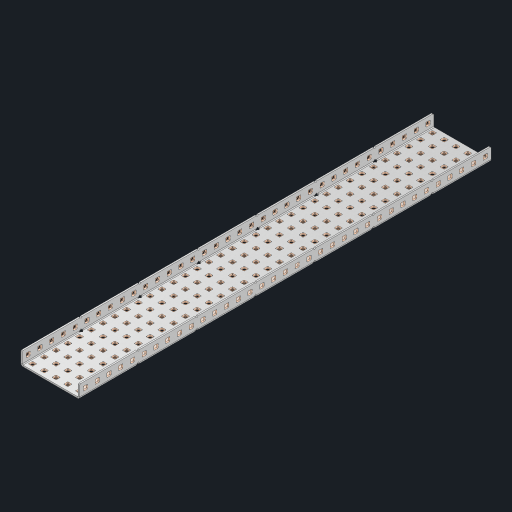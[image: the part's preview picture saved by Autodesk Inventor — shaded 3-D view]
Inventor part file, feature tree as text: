
AUTODESK INVENTOR PART (.ipt)
format: ipt  version: 2023 (Build 270158000, 158)  size: 2,543,616 bytes
history: native  units: in
note: dims shown in document units (in); Inventor stores cm internally (conversion verified against a paired STEP export)
features: other x250, extrude x244, sheet_metal_op x10, sketch x8, mirror x1, pattern_linear x1, chamfer x1
ambient origin geometry x8: Origin, YZ Plane, XZ Plane, XY Plane, X Axis, Y Axis, Z Axis, Center Point
bodies: Solid1 (feature_tree), Body (feature_tree)
feature tree (515):
  other  "Flange Pattern Plane"
  sheet_metal_op  "Flange Pattern"
  sheet_metal_op  "Body Pattern"
  other  "Arc Length"
  mirror  "Notch Mirror"
  pattern_linear  "Notch Pattern"  Spacing1=0.25in  [1 undecoded]
  chamfer  "End Chamfer"
  extrude  "Half Cut"  Depth=0.0625in
  sketch  "Sketch1"  dims[d0=2.5in]
  other  "Plate1"
  sketch  "Sketch2"  dims[d1=17.5in]
  other  "Plate2"
  sheet_metal_op  "Bend1"
  sheet_metal_op  "Corner1"
  sketch  "Sketch3"  dims[d2=0.0625in]
  other  "Flange Pattern Sketch"
  sketch  "Sketch7"  dims[d3=0.0625in]
  other  "Srf1"
  other  "Srf2"
  sketch  "Sketch8"  dims[d4=0.0312in]
  sketch  "Sketch9"  dims[d5=0.125in]
  other  "Srf91"
  sheet_metal_op  "Body Pattern Sketch"
  other  "Srf92"
  sketch  "Sketch13"  dims[d6=0.0625in]
  sketch  "Sketch14"  dims[d7=0.5in d8=90.0deg d9=0.0312in d10=0.25in d11=0.0625in d12=0.0625in d16=0.182in d17=0.02in d18=0.0625in d19=0.0in d20=0.25in d21=0.25in d46=0.172in d47=1.0in d48=0.0in d49=0.182in d50=0.02in d51=0.25in d52=0.25in d53=0.0625in d54=0.0in d55=0.172in d56=1.0in d57=0.0in d60=13.7795in d62=0.5in d63=1.9685in d65=0.5in d85=0.1473in d86=0.1782in d88=0.04in d89=0.0625in d90=0.0in d91=0.04in d92=0.0491in d95=2.5in d96=0.04in d97=0.25in d98=45.0deg d101=0.0in d102=2.497in d131=2.5in d132=13.7795in d134=0.5in d139=0.5in]
  other  "Srf856"
  other  "Srf1310"
  other  "Srf1311"
  other  "Srf1312"
  other  "Srf1376"
  other  "Srf1377"
  other  "Srf1728"
  other  "Srf1755"
  other  "Srf1878"
  other  "Srf1879"
  other  "Srf1880"
  other  "Srf1881"
  other  "Srf1882"
  other  "Srf1883"
  other  "Srf1884"
  other  "Srf1885"
  other  "Srf1886"
  other  "Srf1887"
  other  "Srf1888"
  other  "Srf1889"
  other  "Srf1890"
  other  "Srf1891"
  other  "Srf1892"
  other  "Srf1893"
  other  "Srf1894"
  other  "Srf1895"
  other  "Srf1896"
  other  "Srf1897"
  other  "Srf1898"
  other  "Srf1899"
  other  "Srf1900"
  other  "Srf1901"
  other  "Srf1902"
  other  "Srf1903"
  other  "Srf1904"
  other  "Srf1905"
  other  "Srf1906"
  other  "Srf1942"
  other  "Srf1943"
  other  "Srf1944"
  other  "Srf1945"
  other  "Srf1946"
  other  "Srf1947"
  other  "Srf1948"
  other  "Srf1949"
  other  "Srf1950"
  other  "Srf1951"
  other  "Srf1952"
  other  "Srf1953"
  other  "Srf1954"
  other  "Srf1955"
  other  "Srf1956"
  other  "Srf1957"
  other  "Srf1958"
  other  "Srf1959"
  other  "Srf1960"
  other  "Srf1961"
  other  "Srf1962"
  other  "Srf1963"
  other  "Srf1964"
  other  "Srf1965"
  other  "Srf1966"
  other  "Srf1967"
  other  "Srf1968"
  other  "Srf1969"
  other  "Srf1970"
  other  "Srf2111"
  other  "Srf2112"
  other  "Srf2113"
  other  "Srf2114"
  other  "Srf2115"
  other  "Srf2116"
  other  "Srf2117"
  other  "Srf2118"
  other  "Srf2119"
  other  "Srf2120"
  other  "Srf2121"
  other  "Srf2122"
  other  "Srf2123"
  other  "Srf2124"
  other  "Srf2125"
  other  "Srf2126"
  other  "Srf2127"
  other  "Srf2128"
  other  "Srf2129"
  other  "Srf2130"
  other  "Srf2131"
  other  "Srf2132"
  other  "Srf2133"
  other  "Srf2134"
  other  "Srf2135"
  other  "Srf2136"
  other  "Srf2137"
  other  "Srf2138"
  other  "Srf2139"
  other  "Srf2140"
  other  "Srf2141"
  other  "Srf2142"
  other  "Srf2143"
  other  "Srf2144"
  other  "Srf2145"
  other  "Srf2146"
  other  "Srf2147"
  other  "Srf2148"
  other  "Srf2149"
  other  "Srf2150"
  other  "Srf2151"
  other  "Srf2152"
  other  "Srf2153"
  other  "Srf2154"
  other  "Srf2155"
  other  "Srf2156"
  other  "Srf2157"
  other  "Srf2158"
  other  "Srf2159"
  other  "Srf2160"
  other  "Srf2161"
  other  "Srf2162"
  other  "Srf2163"
  other  "Srf2164"
  other  "Srf2165"
  other  "Srf2166"
  other  "Srf2167"
  other  "Srf2168"
  other  "Srf2169"
  other  "Srf2170"
  other  "Srf2171"
  other  "Srf2172"
  other  "Srf2173"
  other  "Srf2174"
  other  "Srf2175"
  other  "Srf2176"
  other  "Srf2177"
  other  "Srf2178"
  other  "Srf2179"
  other  "Srf2180"
  other  "Srf2181"
  other  "Srf2182"
  other  "Srf2183"
  other  "Srf2184"
  other  "Srf2185"
  other  "Srf2186"
  other  "Srf2187"
  other  "Srf2188"
  other  "Srf2189"
  other  "Srf2190"
  other  "Srf2191"
  other  "Srf2192"
  other  "Srf2193"
  other  "Srf2194"
  other  "Srf2195"
  other  "Srf2196"
  other  "Srf2197"
  other  "Srf2198"
  other  "Srf2199"
  other  "Srf2200"
  other  "Srf2201"
  other  "Srf2202"
  other  "Srf2203"
  other  "Srf2204"
  other  "Srf2205"
  other  "Srf2206"
  other  "Srf2207"
  other  "Srf2208"
  other  "Srf2209"
  other  "Srf2210"
  other  "Srf2211"
  other  "Srf2212"
  other  "Srf2213"
  other  "Srf2214"
  other  "Srf2215"
  other  "Srf2216"
  other  "Srf2217"
  other  "Srf2218"
  other  "Srf2219"
  other  "Srf2220"
  other  "Srf2221"
  other  "Srf2222"
  other  "Srf2223"
  other  "Srf2224"
  other  "Srf2225"
  other  "Srf2226"
  other  "Srf2227"
  other  "Srf2228"
  other  "Srf2229"
  other  "Srf2230"
  other  "Srf2231"
  other  "Srf2232"
  other  "Srf2233"
  other  "Srf2234"
  other  "Srf2235"
  other  "Srf2236"
  other  "Srf2237"
  other  "Srf2238"
  other  "Srf2239"
  other  "Srf2240"
  other  "Srf2241"
  other  "Srf2242"
  other  "Srf2243"
  other  "Srf2244"
  other  "Srf2245"
  other  "Srf2246"
  other  "Srf2247"
  other  "Srf2248"
  other  "Srf2249"
  other  "Srf2250"
  other  "Srf2251"
  other  "Srf2252"
  other  "Srf2253"
  other  "Srf2254"
  other  "Srf2255"
  other  "Srf2256"
  other  "Srf2257"
  other  "Srf2258"
  other  "Srf2259"
  other  "Srf2260"
  other  "Srf2261"
  other  "Srf2262"
  other  "Srf2263"
  other  "Srf2264"
  other  "Srf2265"
  other  "Srf2266"
  other  "Srf2267"
  other  "Srf2268"
  other  "Srf2269"
  other  "Srf2270"
  other  "Srf2271"
  other  "Srf2272"
  other  "Srf2273"
  other  "Srf2274"
  other  "Srf2275"
  other  "Srf2276"
  other  "Srf2277"
  other  "Srf2278"
  other  "Srf2279"
  other  "Srf2280"
  other  "Srf2281"
  other  "Srf2282"
  other  "Srf2283"
  other  "Srf2284"
  other  "Srf2285"
  sheet_metal_op  "Flange Stamp"
  sheet_metal_op  "Flange Circle"
  sheet_metal_op  "Body Stamp"
  sheet_metal_op  "Body Circle"
  sheet_metal_op  "Notch"
  extrude  "ExtrusionSrf2"  Depth=0.0625in
  extrude  "ExtrusionSrf92"  Depth=2.5in
  extrude  "ExtrusionSrf856"  Depth=0.02in
  extrude  "ExtrusionSrf1310"  Depth=0.0625in
  extrude  "ExtrusionSrf1311"  TaperAngle=0.0deg  [1 undecoded]
  extrude  "ExtrusionSrf1312"  Depth=0.25in
  extrude  "ExtrusionSrf1376"  Depth=0.25in
  extrude  "ExtrusionSrf1377"  Depth=2.5in
  extrude  "ExtrusionSrf1728"  Depth=2.5in TaperAngle=0.0deg
  extrude  "ExtrusionSrf1755"  Depth=2.5in
  extrude  "ExtrusionSrf1878"  Depth=0.02in
  extrude  "ExtrusionSrf1879"  Depth=0.25in
  extrude  "ExtrusionSrf1880"  Depth=0.25in
  extrude  "ExtrusionSrf1881"  Depth=0.0625in
  extrude  "ExtrusionSrf1882"  TaperAngle=0.0deg  [1 undecoded]
  extrude  "ExtrusionSrf1883"  Depth=2.5in
  extrude  "ExtrusionSrf1884"  Depth=2.5in TaperAngle=0.0deg
  extrude  "ExtrusionSrf1885"  Depth=2.5in
  extrude  "ExtrusionSrf1886"  Depth=2.5in
  extrude  "ExtrusionSrf1887"  Depth=2.5in
  extrude  "ExtrusionSrf1888"  Depth=2.5in
  extrude  "ExtrusionSrf1889"  Depth=2.5in
  extrude  "ExtrusionSrf1890"  Depth=0.0625in
  extrude  "ExtrusionSrf1891"  TaperAngle=0.0deg  [1 undecoded]
  extrude  "ExtrusionSrf1892"  Depth=2.5in
  extrude  "ExtrusionSrf1893"  Depth=2.5in
  extrude  "ExtrusionSrf1894"  Depth=2.5in
  extrude  "ExtrusionSrf1895"  Depth=0.25in TaperAngle=45.0deg
  extrude  "ExtrusionSrf1896"  TaperAngle=0.0deg  [1 undecoded]
  extrude  "ExtrusionSrf1897"  Depth=2.5in
  extrude  "ExtrusionSrf1898"  Depth=2.5in
  extrude  "ExtrusionSrf1899"  Depth=2.5in
  extrude  "ExtrusionSrf1900"  Depth=2.5in
  extrude  "ExtrusionSrf1901"  Depth=2.5in
  extrude  "ExtrusionSrf1902"  [1 undecoded]
  extrude  "ExtrusionSrf1903"  [1 undecoded]
  extrude  "ExtrusionSrf1904"  [1 undecoded]
  extrude  "ExtrusionSrf1905"  [1 undecoded]
  extrude  "ExtrusionSrf1906"  [1 undecoded]
  extrude  "ExtrusionSrf1942"  [1 undecoded]
  extrude  "ExtrusionSrf1943"  [1 undecoded]
  extrude  "ExtrusionSrf1944"  [1 undecoded]
  extrude  "ExtrusionSrf1945"  [1 undecoded]
  extrude  "ExtrusionSrf1946"  [1 undecoded]
  extrude  "ExtrusionSrf1947"  [1 undecoded]
  extrude  "ExtrusionSrf1948"  [1 undecoded]
  extrude  "ExtrusionSrf1949"  [1 undecoded]
  extrude  "ExtrusionSrf1950"  [1 undecoded]
  extrude  "ExtrusionSrf1951"  [1 undecoded]
  extrude  "ExtrusionSrf1952"  [1 undecoded]
  extrude  "ExtrusionSrf1953"  [1 undecoded]
  extrude  "ExtrusionSrf1954"  [1 undecoded]
  extrude  "ExtrusionSrf1955"  [1 undecoded]
  extrude  "ExtrusionSrf1956"  [1 undecoded]
  extrude  "ExtrusionSrf1957"  [1 undecoded]
  extrude  "ExtrusionSrf1958"  [1 undecoded]
  extrude  "ExtrusionSrf1959"  [1 undecoded]
  extrude  "ExtrusionSrf1960"  [1 undecoded]
  extrude  "ExtrusionSrf1961"  [1 undecoded]
  extrude  "ExtrusionSrf1962"  [1 undecoded]
  extrude  "ExtrusionSrf1963"  [1 undecoded]
  extrude  "ExtrusionSrf1964"  [1 undecoded]
  extrude  "ExtrusionSrf1965"  [1 undecoded]
  extrude  "ExtrusionSrf1966"  [1 undecoded]
  extrude  "ExtrusionSrf1967"  [1 undecoded]
  extrude  "ExtrusionSrf1968"  [1 undecoded]
  extrude  "ExtrusionSrf1969"  [1 undecoded]
  extrude  "ExtrusionSrf1970"  [1 undecoded]
  extrude  "ExtrusionSrf2111"  [1 undecoded]
  extrude  "ExtrusionSrf2112"  [1 undecoded]
  extrude  "ExtrusionSrf2113"  [1 undecoded]
  extrude  "ExtrusionSrf2114"  [1 undecoded]
  extrude  "ExtrusionSrf2115"  [1 undecoded]
  extrude  "ExtrusionSrf2116"  [1 undecoded]
  extrude  "ExtrusionSrf2117"  [1 undecoded]
  extrude  "ExtrusionSrf2118"  [1 undecoded]
  extrude  "ExtrusionSrf2119"  [1 undecoded]
  extrude  "ExtrusionSrf2120"  [1 undecoded]
  extrude  "ExtrusionSrf2121"  [1 undecoded]
  extrude  "ExtrusionSrf2122"  [1 undecoded]
  extrude  "ExtrusionSrf2123"  [1 undecoded]
  extrude  "ExtrusionSrf2124"  [1 undecoded]
  extrude  "ExtrusionSrf2125"  [1 undecoded]
  extrude  "ExtrusionSrf2126"  [1 undecoded]
  extrude  "ExtrusionSrf2127"  [1 undecoded]
  extrude  "ExtrusionSrf2128"  [1 undecoded]
  extrude  "ExtrusionSrf2129"  [1 undecoded]
  extrude  "ExtrusionSrf2130"  [1 undecoded]
  extrude  "ExtrusionSrf2131"  [1 undecoded]
  extrude  "ExtrusionSrf2132"  [1 undecoded]
  extrude  "ExtrusionSrf2133"  [1 undecoded]
  extrude  "ExtrusionSrf2134"  [1 undecoded]
  extrude  "ExtrusionSrf2135"  [1 undecoded]
  extrude  "ExtrusionSrf2136"  [1 undecoded]
  extrude  "ExtrusionSrf2137"  [1 undecoded]
  extrude  "ExtrusionSrf2138"  [1 undecoded]
  extrude  "ExtrusionSrf2139"  [1 undecoded]
  extrude  "ExtrusionSrf2140"  [1 undecoded]
  extrude  "ExtrusionSrf2141"  [1 undecoded]
  extrude  "ExtrusionSrf2142"  [1 undecoded]
  extrude  "ExtrusionSrf2143"  [1 undecoded]
  extrude  "ExtrusionSrf2144"  [1 undecoded]
  extrude  "ExtrusionSrf2145"  [1 undecoded]
  extrude  "ExtrusionSrf2146"  [1 undecoded]
  extrude  "ExtrusionSrf2147"  [1 undecoded]
  extrude  "ExtrusionSrf2148"  [1 undecoded]
  extrude  "ExtrusionSrf2149"  [1 undecoded]
  extrude  "ExtrusionSrf2150"  [1 undecoded]
  extrude  "ExtrusionSrf2151"  [1 undecoded]
  extrude  "ExtrusionSrf2152"  [1 undecoded]
  extrude  "ExtrusionSrf2153"  [1 undecoded]
  extrude  "ExtrusionSrf2154"  [1 undecoded]
  extrude  "ExtrusionSrf2155"  [1 undecoded]
  extrude  "ExtrusionSrf2156"  [1 undecoded]
  extrude  "ExtrusionSrf2157"  [1 undecoded]
  extrude  "ExtrusionSrf2158"  [1 undecoded]
  extrude  "ExtrusionSrf2159"  [1 undecoded]
  extrude  "ExtrusionSrf2160"  [1 undecoded]
  extrude  "ExtrusionSrf2161"  [1 undecoded]
  extrude  "ExtrusionSrf2162"  [1 undecoded]
  extrude  "ExtrusionSrf2163"  [1 undecoded]
  extrude  "ExtrusionSrf2164"  [1 undecoded]
  extrude  "ExtrusionSrf2165"  [1 undecoded]
  extrude  "ExtrusionSrf2166"  [1 undecoded]
  extrude  "ExtrusionSrf2167"  [1 undecoded]
  extrude  "ExtrusionSrf2168"  [1 undecoded]
  extrude  "ExtrusionSrf2169"  [1 undecoded]
  extrude  "ExtrusionSrf2170"  [1 undecoded]
  extrude  "ExtrusionSrf2171"  [1 undecoded]
  extrude  "ExtrusionSrf2172"  [1 undecoded]
  extrude  "ExtrusionSrf2173"  [1 undecoded]
  extrude  "ExtrusionSrf2174"  [1 undecoded]
  extrude  "ExtrusionSrf2175"  [1 undecoded]
  extrude  "ExtrusionSrf2176"  [1 undecoded]
  extrude  "ExtrusionSrf2177"  [1 undecoded]
  extrude  "ExtrusionSrf2178"  [1 undecoded]
  extrude  "ExtrusionSrf2179"  [1 undecoded]
  extrude  "ExtrusionSrf2180"  [1 undecoded]
  extrude  "ExtrusionSrf2181"  [1 undecoded]
  extrude  "ExtrusionSrf2182"  [1 undecoded]
  extrude  "ExtrusionSrf2183"  [1 undecoded]
  extrude  "ExtrusionSrf2184"  [1 undecoded]
  extrude  "ExtrusionSrf2185"  [1 undecoded]
  extrude  "ExtrusionSrf2186"  [1 undecoded]
  extrude  "ExtrusionSrf2187"  [1 undecoded]
  extrude  "ExtrusionSrf2188"  [1 undecoded]
  extrude  "ExtrusionSrf2189"  [1 undecoded]
  extrude  "ExtrusionSrf2190"  [1 undecoded]
  extrude  "ExtrusionSrf2191"  [1 undecoded]
  extrude  "ExtrusionSrf2192"  [1 undecoded]
  extrude  "ExtrusionSrf2193"  [1 undecoded]
  extrude  "ExtrusionSrf2194"  [1 undecoded]
  extrude  "ExtrusionSrf2195"  [1 undecoded]
  extrude  "ExtrusionSrf2196"  [1 undecoded]
  extrude  "ExtrusionSrf2197"  [1 undecoded]
  extrude  "ExtrusionSrf2198"  [1 undecoded]
  extrude  "ExtrusionSrf2199"  [1 undecoded]
  extrude  "ExtrusionSrf2200"  [1 undecoded]
  extrude  "ExtrusionSrf2201"  [1 undecoded]
  extrude  "ExtrusionSrf2202"  [1 undecoded]
  extrude  "ExtrusionSrf2203"  [1 undecoded]
  extrude  "ExtrusionSrf2204"  [1 undecoded]
  extrude  "ExtrusionSrf2205"  [1 undecoded]
  extrude  "ExtrusionSrf2206"  [1 undecoded]
  extrude  "ExtrusionSrf2207"  [1 undecoded]
  extrude  "ExtrusionSrf2208"  [1 undecoded]
  extrude  "ExtrusionSrf2209"  [1 undecoded]
  extrude  "ExtrusionSrf2210"  [1 undecoded]
  extrude  "ExtrusionSrf2211"  [1 undecoded]
  extrude  "ExtrusionSrf2212"  [1 undecoded]
  extrude  "ExtrusionSrf2213"  [1 undecoded]
  extrude  "ExtrusionSrf2214"  [1 undecoded]
  extrude  "ExtrusionSrf2215"  [1 undecoded]
  extrude  "ExtrusionSrf2216"  [1 undecoded]
  extrude  "ExtrusionSrf2217"  [1 undecoded]
  extrude  "ExtrusionSrf2218"  [1 undecoded]
  extrude  "ExtrusionSrf2219"  [1 undecoded]
  extrude  "ExtrusionSrf2220"  [1 undecoded]
  extrude  "ExtrusionSrf2221"  [1 undecoded]
  extrude  "ExtrusionSrf2222"  [1 undecoded]
  extrude  "ExtrusionSrf2223"  [1 undecoded]
  extrude  "ExtrusionSrf2224"  [1 undecoded]
  extrude  "ExtrusionSrf2225"  [1 undecoded]
  extrude  "ExtrusionSrf2226"  [1 undecoded]
  extrude  "ExtrusionSrf2227"  [1 undecoded]
  extrude  "ExtrusionSrf2228"  [1 undecoded]
  extrude  "ExtrusionSrf2229"  [1 undecoded]
  extrude  "ExtrusionSrf2230"  [1 undecoded]
  extrude  "ExtrusionSrf2231"  [1 undecoded]
  extrude  "ExtrusionSrf2232"  [1 undecoded]
  extrude  "ExtrusionSrf2233"  [1 undecoded]
  extrude  "ExtrusionSrf2234"  [1 undecoded]
  extrude  "ExtrusionSrf2235"  [1 undecoded]
  extrude  "ExtrusionSrf2236"  [1 undecoded]
  extrude  "ExtrusionSrf2237"  [1 undecoded]
  extrude  "ExtrusionSrf2238"  [1 undecoded]
  extrude  "ExtrusionSrf2239"  [1 undecoded]
  extrude  "ExtrusionSrf2240"  [1 undecoded]
  extrude  "ExtrusionSrf2241"  [1 undecoded]
  extrude  "ExtrusionSrf2242"  [1 undecoded]
  extrude  "ExtrusionSrf2243"  [1 undecoded]
  extrude  "ExtrusionSrf2244"  [1 undecoded]
  extrude  "ExtrusionSrf2245"  [1 undecoded]
  extrude  "ExtrusionSrf2246"  [1 undecoded]
  extrude  "ExtrusionSrf2247"  [1 undecoded]
  extrude  "ExtrusionSrf2248"  [1 undecoded]
  extrude  "ExtrusionSrf2249"  [1 undecoded]
  extrude  "ExtrusionSrf2250"  [1 undecoded]
  extrude  "ExtrusionSrf2251"  [1 undecoded]
  extrude  "ExtrusionSrf2252"  [1 undecoded]
  extrude  "ExtrusionSrf2253"  [1 undecoded]
  extrude  "ExtrusionSrf2254"  [1 undecoded]
  extrude  "ExtrusionSrf2255"  [1 undecoded]
  extrude  "ExtrusionSrf2256"  [1 undecoded]
  extrude  "ExtrusionSrf2257"  [1 undecoded]
  extrude  "ExtrusionSrf2258"  [1 undecoded]
  extrude  "ExtrusionSrf2259"  [1 undecoded]
  extrude  "ExtrusionSrf2260"  [1 undecoded]
  extrude  "ExtrusionSrf2261"  [1 undecoded]
  extrude  "ExtrusionSrf2262"  [1 undecoded]
  extrude  "ExtrusionSrf2263"  [1 undecoded]
  extrude  "ExtrusionSrf2264"  [1 undecoded]
  extrude  "ExtrusionSrf2265"  [1 undecoded]
  extrude  "ExtrusionSrf2266"  [1 undecoded]
  extrude  "ExtrusionSrf2267"  [1 undecoded]
  extrude  "ExtrusionSrf2268"  [1 undecoded]
  extrude  "ExtrusionSrf2269"  [1 undecoded]
  extrude  "ExtrusionSrf2270"  [1 undecoded]
  extrude  "ExtrusionSrf2271"  [1 undecoded]
  extrude  "ExtrusionSrf2272"  [1 undecoded]
  extrude  "ExtrusionSrf2273"  [1 undecoded]
  extrude  "ExtrusionSrf2274"  [1 undecoded]
  extrude  "ExtrusionSrf2275"  [1 undecoded]
  extrude  "ExtrusionSrf2276"  [1 undecoded]
  extrude  "ExtrusionSrf2277"  [1 undecoded]
  extrude  "ExtrusionSrf2278"  [1 undecoded]
  extrude  "ExtrusionSrf2279"  [1 undecoded]
  extrude  "ExtrusionSrf2280"  [1 undecoded]
  extrude  "ExtrusionSrf2281"  [1 undecoded]
  extrude  "ExtrusionSrf2282"  [1 undecoded]
  extrude  "ExtrusionSrf2283"  [1 undecoded]
  extrude  "ExtrusionSrf2284"  [1 undecoded]
  extrude  "ExtrusionSrf2285"  [1 undecoded]
note: 214 required parameter values undecoded (feature->parameter linkage not recoverable at this tier; creation-order binding heuristic only, values carry confidence <= 0.55)
